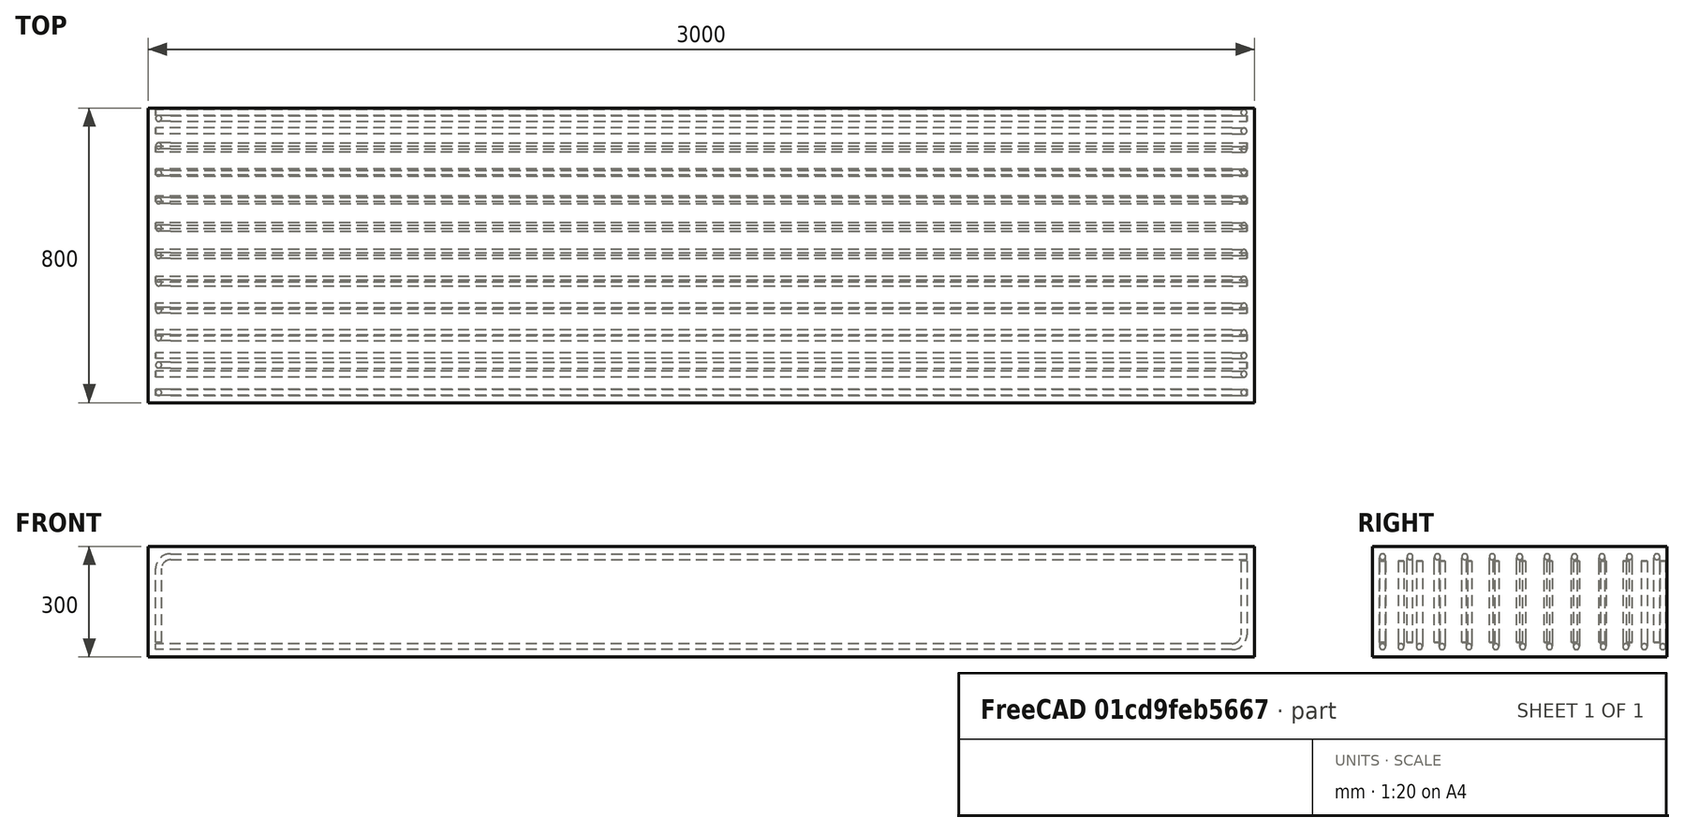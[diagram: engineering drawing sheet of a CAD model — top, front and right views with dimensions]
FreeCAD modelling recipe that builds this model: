
FCSTD DOCUMENT  (FreeCAD 0.19R20802 (Git))
Label: lshape_rebar_drawing_dimensioning
License: All rights reserved
LicenseURL: http://en.wikipedia.org/wiki/All_rights_reserved
objects: TechDraw::DrawViewSymbolPython×18, TechDraw::DrawSVGTemplate×6, TechDraw::DrawPage×6, Part::FeaturePython×3, Sketcher::SketchObject×2
note: 5 computed .brp shape members not serialized (recipe doc carries the construction recipe); baked Part::Feature solids carry a one-line shape summary decoded from their .brp

FEATURE [Part::FeaturePython] Structure  label="Footing"  # Arch/BIM 77 (typed FeaturePython)
  FaceMaker = 0
  Height = 300
  HorizontalArea = 2400000
  IfcData = attributes={"GlobalId": {"name": "GlobalId", "type": "IfcGloballyUniqueId", "is_enum": false, "enum_values": []}, "Description": {"... (+505 chars omitted),+1 more (map truncated)
  IfcType = 77
  Length = 3000
  MoveBase = false
  MoveWithHost = false
  Nodes = (2) [(0,0,5.55112e-16),(0,0,3000)]
  NodesOffset = 0
  Normal = (0,0,0)
  PerimeterLength = 7600
  PredefinedType = 1
  VerticalArea = 2280000
  Width = 800
FEATURE [Sketcher::SketchObject] Sketch
  MapMode = 5
  Placement = pos=(0,-400,0) rot=(1,0,0;1.5708rad)
  Support = -> [Structure]
  sketch-geometry (2):
    g0: LineSegment StartX=2972 StartY=110 StartZ=0 EndX=2972 EndY=-122 EndZ=0
    g1: LineSegment StartX=2972 StartY=-122 StartZ=0 EndX=20 EndY=-122 EndZ=0
FEATURE [Part::FeaturePython] Rebar  label="LShapeRebar"  # Arch/BIM 110 (typed FeaturePython)
  Amount = 13
  AmountCheck = false
  Base = -> Sketch
  BottomCover = 20
  CustomSpacing = 3@50.0+7@72.85714285714286+3@50.0
  Diameter = 16
  Direction = (0,0,0)
  Distance = 0
  FrontCover = 20
  HorizontalArea = 0
  Host = -> Structure
  IfcType = 110
  LeftCover = 20
  Length = 3184
  Mark = BRb
  MoveBase = false
  MoveWithHost = false
  OffsetEnd = 28
  OffsetStart = 28
  Orientation = Bottom Right
  PerimeterLength = 0
  PlacementList = 13 placements: [(0,28,-6.21725e-15),(0,78,-1.73195e-14),(0,128,-2.84217e-14),(0,189.429,-4.20616e-14),(0,262.286,-5.82391e-14),(0,335.143,-7.44167e-14),(0,408,-9.05942e-14),(0,480.857,-1.06772e-13),(0,553.714,-1.22949e-13),(0,626.571,-1.39127e-13),(0,688,-1.52767e-13),(0,738,-1.63869e-13),(0,788,-1.74971e-13)]
  RebarShape = 2
  RightCover = 20
  Rounding = 2
  Spacing = 0
  TopCover = 40
  TotalLength = 41392
  TrueSpacing = 50
  VerticalArea = 0
FEATURE [Sketcher::SketchObject] Sketch001
  MapMode = 5
  Placement = pos=(0,-400,0) rot=(1,0,0;1.5708rad)
  Support = -> [Structure]
  sketch-geometry (2):
    g0: LineSegment StartX=28 StartY=-110 StartZ=0 EndX=28 EndY=122 EndZ=0
    g1: LineSegment StartX=28 StartY=122 StartZ=0 EndX=2980 EndY=122 EndZ=0
FEATURE [Part::FeaturePython] Rebar001  label="LShapeRebar001"  # Arch/BIM 110 (typed FeaturePython)
  Amount = 11
  AmountCheck = false
  Base = -> Sketch001
  BottomCover = 40
  Diameter = 16
  Direction = (0,0,0)
  Distance = 0
  FrontCover = 20
  HorizontalArea = 0
  Host = -> Structure
  IfcType = 110
  LeftCover = 20
  Length = 3184
  Mark = TRb
  MoveBase = false
  MoveWithHost = false
  OffsetEnd = 28
  OffsetStart = 28
  Orientation = Top Left
  PerimeterLength = 0
  PlacementList = 11 placements: arithmetic series from (0,28,-6.21725e-15) step (0,74.4,-1.65201e-14) to (0,772,-1.71418e-13)
  RebarShape = 2
  RightCover = 20
  Rounding = 2
  Spacing = 74.4
  TopCover = 20
  TotalLength = 35024
  TrueSpacing = 70
  VerticalArea = 0
FEATURE [TechDraw::DrawSVGTemplate] Template
  Height = 210
  Orientation = 1
  Width = 297
FEATURE [TechDraw::DrawViewSymbolPython] ReinforcementDrawingView  label="Front View"  # drawing view (typed FeaturePython)
  DimensionBottomOffset = 16
  DimensionLeftOffset = 10
  DimensionRightOffset = 10
  DimensionTopOffset = 16
  Height = 300
  LeftOffset = 20
  LockPosition = false
  MaxHeight = 210
  MaxWidth = 297
  MinBottomOffset = 20
  MinRightOffset = 20
  PositionType = 0
  Rebars = -> [Rebar,Rebar001]
  RebarsColorStyle = 0
  RebarsStrokeWidth = 0.35
  Rotation = 0
  Scale = 0.0856667
  ScaleType = 1
  Structure = -> Structure
  StructureColorStyle = 0
  StructureStrokeWidth = 0.5
  Symbol = <blob: 3186 chars omitted>
  Template = -> Template
  TopOffset = 92.15
  View = 0
  VisibleRebars = -> [Rebar,Rebar001]
  Width = 3000
  X = 148.5
  Y = 105
  expr: TopOffset = .Template.Height.Value / 2 - .Height.Value * .Scale / 2
  expr: LeftOffset = .Template.Width.Value / 2 - .Width.Value * .Scale / 2
FEATURE [TechDraw::DrawViewSymbolPython] ReinforcementDimensioning  # drawing view (typed FeaturePython)
  DimensionBottomOffset = 10
  DimensionFormat = %M %C⌀%D,span=%S
  DimensionLeftOffset = 10
  DimensionRightOffset = 10
  DimensionTopOffset = 10
  Font = DejaVu Sans
  FontSize = 3
  LineEndSymbol = 0
  LineMidPointSymbol = 1
  LineStartSymbol = 3
  LineStyle = 0
  LockPosition = false
  MultiRebar_LineEndSymbol = 0
  MultiRebar_LineStartSymbol = 0
  MultiRebar_OuterDimension = true
  MultiRebar_TextPositionType = 0
  ParentDrawingView = -> ReinforcementDrawingView
  Rebar = -> Rebar
  Rotation = 0
  Scale = 0.0856667
  ScaleType = 2
  SingleRebar_LineEndSymbol = 0
  SingleRebar_LineStartSymbol = 3
  SingleRebar_OuterDimension = false
  SingleRebar_TextPositionType = 1
  StrokeWidth = 0.25
  Symbol = <svg version="1.1" xmlns="http://www.w3.org/2000/svg" xmlns:xlink="http://www.w3.org/1999/xlink" xmlns:freecad="http://www.freecadweb.org/wiki/index.php?title=Svg_Namespace" width="3000.0mm" height="300.0mm" viewBox="0 0 3000.0 300.0"><g transform="translate(0.0, 150.00000000000065)"><g><path d="M609.0 266.7315175097276 L609.0 121.99999999999966" style="stroke:#00007f;stroke-width:2.9182879377431905;stroke-linecap:round;fill:none;" stroke-dasharray="" /><g id="line_mid_points" /><path d="M0,0 -8,-1.5 V1.5 L0,0" style="stroke:#00007f;fill:#00007f;stroke-width:2.9182879377431905;stroke-linecap:round;stroke-linejoin:bevel;" transform="translate(609.0 121.99999999999966) rotate(-90.0 0 0)" /></g><text x="609.0" y="284.24124513618676" style="white-space:pre;" fill="#005400" font-family="DejaVu Sans" font-size="35.019455252918284" text-anchor="middle" dominant-baseline="baseline" xml:space="preserve">BRb 13⌀16,span=760</text></g></svg>
  TextPositionType = 0
  WayPoints = (2) [(0,0,0),(50,0,0)]
  WayPointsType = 0
  X = 148.5
  Y = 105
FEATURE [TechDraw::DrawViewSymbolPython] ReinforcementDimensioning001  # drawing view (typed FeaturePython)
  DimensionBottomOffset = 16
  DimensionFormat = %M %C⌀%D,span=%S
  DimensionLeftOffset = 10
  DimensionRightOffset = 10
  DimensionTopOffset = 10
  Font = DejaVu Sans
  FontSize = 3
  LineEndSymbol = 0
  LineMidPointSymbol = 1
  LineStartSymbol = 3
  LineStyle = 0
  LockPosition = false
  MultiRebar_LineEndSymbol = 0
  MultiRebar_LineStartSymbol = 0
  MultiRebar_OuterDimension = true
  MultiRebar_TextPositionType = 0
  ParentDrawingView = -> ReinforcementDrawingView
  Rebar = -> Rebar001
  Rotation = 0
  Scale = 0.0856667
  ScaleType = 2
  SingleRebar_LineEndSymbol = 0
  SingleRebar_LineStartSymbol = 3
  SingleRebar_OuterDimension = false
  SingleRebar_TextPositionType = 1
  StrokeWidth = 0.25
  Symbol = <svg version="1.1" xmlns="http://www.w3.org/2000/svg" xmlns:xlink="http://www.w3.org/1999/xlink" xmlns:freecad="http://www.freecadweb.org/wiki/index.php?title=Svg_Namespace" width="3000.0mm" height="300.0mm" viewBox="0 0 3000.0 300.0"><g transform="translate(0.0, 150.00000000000065)"><g><path d="M2530.0 -266.7315175097283 L2530.0 -122.00000000000034" style="stroke:#00007f;stroke-width:2.9182879377431905;stroke-linecap:round;fill:none;" stroke-dasharray="" /><g id="line_mid_points" /><path d="M0,0 -8,-1.5 V1.5 L0,0" style="stroke:#00007f;fill:#00007f;stroke-width:2.9182879377431905;stroke-linecap:round;stroke-linejoin:bevel;" transform="translate(2530.0 -122.00000000000034) rotate(90.0 0 0)" /></g><text x="2530.0" y="-266.7315175097283" style="white-space:pre;" fill="#005400" font-family="DejaVu Sans" font-size="35.019455252918284" text-anchor="middle" dominant-baseline="baseline" xml:space="preserve">TRb 11⌀16,span=744</text></g></svg>
  TextPositionType = 0
  WayPoints = (2) [(0,0,0),(50,0,0)]
  WayPointsType = 0
  X = 148.5
  Y = 105
FEATURE [TechDraw::DrawPage] TechDraw__DrawPage  label="Footing Drawing"
  KeepUpdated = true
  NextBalloonIndex = 1
  ProjectionType = 0
  Template = -> Template
  Views = -> [ReinforcementDrawingView,ReinforcementDimensioning,ReinforcementDimensioning001]
FEATURE [TechDraw::DrawSVGTemplate] Template001
  Height = 210
  Orientation = 1
  Width = 297
FEATURE [TechDraw::DrawViewSymbolPython] ReinforcementDrawingView001  label="Rear View"  # drawing view (typed FeaturePython)
  DimensionBottomOffset = 16
  DimensionLeftOffset = 10
  DimensionRightOffset = 10
  DimensionTopOffset = 16
  Height = 300
  LeftOffset = 20
  LockPosition = false
  MaxHeight = 210
  MaxWidth = 297
  MinBottomOffset = 20
  MinRightOffset = 20
  PositionType = 0
  Rebars = -> [Rebar,Rebar001]
  RebarsColorStyle = 0
  RebarsStrokeWidth = 0.35
  Rotation = 0
  Scale = 0.0856667
  ScaleType = 1
  Structure = -> Structure
  StructureColorStyle = 0
  StructureStrokeWidth = 0.5
  Symbol = <blob: 3214 chars omitted>
  Template = -> Template001
  TopOffset = 92.15
  View = 1
  VisibleRebars = -> [Rebar,Rebar001]
  Width = 3000
  X = 148.5
  Y = 105
  expr: TopOffset = .Template.Height.Value / 2 - .Height.Value * .Scale / 2
  expr: LeftOffset = .Template.Width.Value / 2 - .Width.Value * .Scale / 2
FEATURE [TechDraw::DrawViewSymbolPython] ReinforcementDimensioning002  # drawing view (typed FeaturePython)
  DimensionBottomOffset = 10
  DimensionFormat = %M %C⌀%D,span=%S
  DimensionLeftOffset = 10
  DimensionRightOffset = 10
  DimensionTopOffset = 10
  Font = DejaVu Sans
  FontSize = 3
  LineEndSymbol = 0
  LineMidPointSymbol = 1
  LineStartSymbol = 3
  LineStyle = 0
  LockPosition = false
  MultiRebar_LineEndSymbol = 0
  MultiRebar_LineStartSymbol = 0
  MultiRebar_OuterDimension = true
  MultiRebar_TextPositionType = 0
  ParentDrawingView = -> ReinforcementDrawingView001
  Rebar = -> Rebar
  Rotation = 0
  Scale = 0.0856667
  ScaleType = 2
  SingleRebar_LineEndSymbol = 0
  SingleRebar_LineStartSymbol = 3
  SingleRebar_OuterDimension = false
  SingleRebar_TextPositionType = 1
  StrokeWidth = 0.25
  Symbol = <svg version="1.1" xmlns="http://www.w3.org/2000/svg" xmlns:xlink="http://www.w3.org/1999/xlink" xmlns:freecad="http://www.freecadweb.org/wiki/index.php?title=Svg_Namespace" width="3000.0mm" height="300.0mm" viewBox="0 0 3000.0 300.0"><g transform="translate(3000.0, 150.00000000000065)"><g><path d="M-1851.0 266.7315175097276 L-1851.0 121.99999999999966" style="stroke:#00007f;stroke-width:2.9182879377431905;stroke-linecap:round;fill:none;" stroke-dasharray="" /><g id="line_mid_points" /><path d="M0,0 -8,-1.5 V1.5 L0,0" style="stroke:#00007f;fill:#00007f;stroke-width:2.9182879377431905;stroke-linecap:round;stroke-linejoin:bevel;" transform="translate(-1851.0 121.99999999999966) rotate(-90.0 0 0)" /></g><text x="-1851.0" y="284.24124513618676" style="white-space:pre;" fill="#005400" font-family="DejaVu Sans" font-size="35.019455252918284" text-anchor="middle" dominant-baseline="baseline" xml:space="preserve">BRb 13⌀16,span=760</text></g></svg>
  TextPositionType = 0
  WayPoints = (2) [(0,0,0),(50,0,0)]
  WayPointsType = 0
  X = 148.5
  Y = 105
FEATURE [TechDraw::DrawViewSymbolPython] ReinforcementDimensioning003  # drawing view (typed FeaturePython)
  DimensionBottomOffset = 16
  DimensionFormat = %M %C⌀%D,span=%S
  DimensionLeftOffset = 10
  DimensionRightOffset = 10
  DimensionTopOffset = 10
  Font = DejaVu Sans
  FontSize = 3
  LineEndSymbol = 0
  LineMidPointSymbol = 1
  LineStartSymbol = 3
  LineStyle = 0
  LockPosition = false
  MultiRebar_LineEndSymbol = 0
  MultiRebar_LineStartSymbol = 0
  MultiRebar_OuterDimension = true
  MultiRebar_TextPositionType = 0
  ParentDrawingView = -> ReinforcementDrawingView001
  Rebar = -> Rebar001
  Rotation = 0
  Scale = 0.0856667
  ScaleType = 2
  SingleRebar_LineEndSymbol = 0
  SingleRebar_LineStartSymbol = 3
  SingleRebar_OuterDimension = false
  SingleRebar_TextPositionType = 1
  StrokeWidth = 0.25
  Symbol = <svg version="1.1" xmlns="http://www.w3.org/2000/svg" xmlns:xlink="http://www.w3.org/1999/xlink" xmlns:freecad="http://www.freecadweb.org/wiki/index.php?title=Svg_Namespace" width="3000.0mm" height="300.0mm" viewBox="0 0 3000.0 300.0"><g transform="translate(3000.0, 150.00000000000065)"><g><path d="M-2870.0 -266.7315175097283 L-2870.0 -122.00000000000034" style="stroke:#00007f;stroke-width:2.9182879377431905;stroke-linecap:round;fill:none;" stroke-dasharray="" /><g id="line_mid_points" /><path d="M0,0 -8,-1.5 V1.5 L0,0" style="stroke:#00007f;fill:#00007f;stroke-width:2.9182879377431905;stroke-linecap:round;stroke-linejoin:bevel;" transform="translate(-2870.0 -122.00000000000034) rotate(90.0 0 0)" /></g><text x="-2870.0" y="-266.7315175097283" style="white-space:pre;" fill="#005400" font-family="DejaVu Sans" font-size="35.019455252918284" text-anchor="middle" dominant-baseline="baseline" xml:space="preserve">TRb 11⌀16,span=744</text></g></svg>
  TextPositionType = 0
  WayPoints = (2) [(0,0,0),(50,0,0)]
  WayPointsType = 0
  X = 148.5
  Y = 105
FEATURE [TechDraw::DrawPage] TechDraw__DrawPage001  label="Footing Drawing001"
  KeepUpdated = true
  NextBalloonIndex = 1
  ProjectionType = 0
  Template = -> Template001
  Views = -> [ReinforcementDrawingView001,ReinforcementDimensioning002,ReinforcementDimensioning003]
FEATURE [TechDraw::DrawSVGTemplate] Template002
  Height = 210
  Orientation = 1
  Width = 297
FEATURE [TechDraw::DrawViewSymbolPython] ReinforcementDrawingView002  label="Left View"  # drawing view (typed FeaturePython)
  DimensionBottomOffset = 16
  DimensionLeftOffset = 10
  DimensionRightOffset = 10
  DimensionTopOffset = 16
  Height = 300
  LeftOffset = 20
  LockPosition = false
  MaxHeight = 210
  MaxWidth = 297
  MinBottomOffset = 20
  MinRightOffset = 20
  PositionType = 0
  Rebars = -> [Rebar,Rebar001]
  RebarsColorStyle = 0
  RebarsStrokeWidth = 0.35
  Rotation = 0
  Scale = 0.32125
  ScaleType = 1
  Structure = -> Structure
  StructureColorStyle = 0
  StructureStrokeWidth = 0.5
  Symbol = <blob: 9738 chars omitted>
  Template = -> Template002
  TopOffset = 56.8125
  View = 2
  VisibleRebars = -> [Rebar,Rebar001]
  Width = 800
  X = 148.5
  Y = 105
  expr: TopOffset = .Template.Height.Value / 2 - .Height.Value * .Scale / 2
  expr: LeftOffset = .Template.Width.Value / 2 - .Width.Value * .Scale / 2
FEATURE [TechDraw::DrawViewSymbolPython] ReinforcementDimensioning004  # drawing view (typed FeaturePython)
  DimensionBottomOffset = 10
  DimensionFormat = %M %C⌀%D,span=%S
  DimensionLeftOffset = 10
  DimensionRightOffset = 10
  DimensionTopOffset = 10
  Font = DejaVu Sans
  FontSize = 3
  LineEndSymbol = 0
  LineMidPointSymbol = 1
  LineStartSymbol = 3
  LineStyle = 0
  LockPosition = false
  MultiRebar_LineEndSymbol = 0
  MultiRebar_LineStartSymbol = 0
  MultiRebar_OuterDimension = true
  MultiRebar_TextPositionType = 0
  ParentDrawingView = -> ReinforcementDrawingView002
  Rebar = -> Rebar
  Rotation = 0
  Scale = 0.32125
  ScaleType = 2
  SingleRebar_LineEndSymbol = 0
  SingleRebar_LineStartSymbol = 3
  SingleRebar_OuterDimension = false
  SingleRebar_TextPositionType = 1
  StrokeWidth = 0.25
  Symbol = <blob: 5461 chars omitted>
  TextPositionType = 0
  WayPoints = (2) [(0,0,0),(50,0,0)]
  WayPointsType = 0
  X = 148.5
  Y = 105
FEATURE [TechDraw::DrawViewSymbolPython] ReinforcementDimensioning005  # drawing view (typed FeaturePython)
  DimensionBottomOffset = 16
  DimensionFormat = %M %C⌀%D,span=%S
  DimensionLeftOffset = 10
  DimensionRightOffset = 10
  DimensionTopOffset = 10
  Font = DejaVu Sans
  FontSize = 3
  LineEndSymbol = 0
  LineMidPointSymbol = 1
  LineStartSymbol = 3
  LineStyle = 0
  LockPosition = false
  MultiRebar_LineEndSymbol = 0
  MultiRebar_LineStartSymbol = 0
  MultiRebar_OuterDimension = true
  MultiRebar_TextPositionType = 0
  ParentDrawingView = -> ReinforcementDrawingView002
  Rebar = -> Rebar001
  Rotation = 0
  Scale = 0.32125
  ScaleType = 2
  SingleRebar_LineEndSymbol = 0
  SingleRebar_LineStartSymbol = 3
  SingleRebar_OuterDimension = false
  SingleRebar_TextPositionType = 1
  StrokeWidth = 0.25
  Symbol = <blob: 3041 chars omitted>
  TextPositionType = 0
  WayPoints = (2) [(0,0,0),(50,0,0)]
  WayPointsType = 0
  X = 148.5
  Y = 105
FEATURE [TechDraw::DrawPage] TechDraw__DrawPage002  label="Footing Drawing002"
  KeepUpdated = true
  NextBalloonIndex = 1
  ProjectionType = 0
  Template = -> Template002
  Views = -> [ReinforcementDrawingView002,ReinforcementDimensioning004,ReinforcementDimensioning005]
FEATURE [TechDraw::DrawSVGTemplate] Template003
  Height = 210
  Orientation = 1
  Width = 297
FEATURE [TechDraw::DrawViewSymbolPython] ReinforcementDrawingView003  label="Right View"  # drawing view (typed FeaturePython)
  DimensionBottomOffset = 16
  DimensionLeftOffset = 10
  DimensionRightOffset = 10
  DimensionTopOffset = 16
  Height = 300
  LeftOffset = 20
  LockPosition = false
  MaxHeight = 210
  MaxWidth = 297
  MinBottomOffset = 20
  MinRightOffset = 20
  PositionType = 0
  Rebars = -> [Rebar,Rebar001]
  RebarsColorStyle = 0
  RebarsStrokeWidth = 0.35
  Rotation = 0
  Scale = 0.32125
  ScaleType = 1
  Structure = -> Structure
  StructureColorStyle = 0
  StructureStrokeWidth = 0.5
  Symbol = <blob: 9733 chars omitted>
  Template = -> Template003
  TopOffset = 56.8125
  View = 3
  VisibleRebars = -> [Rebar,Rebar001]
  Width = 800
  X = 148.5
  Y = 105
  expr: TopOffset = .Template.Height.Value / 2 - .Height.Value * .Scale / 2
  expr: LeftOffset = .Template.Width.Value / 2 - .Width.Value * .Scale / 2
FEATURE [TechDraw::DrawViewSymbolPython] ReinforcementDimensioning006  # drawing view (typed FeaturePython)
  DimensionBottomOffset = 10
  DimensionFormat = %M %C⌀%D,span=%S
  DimensionLeftOffset = 10
  DimensionRightOffset = 10
  DimensionTopOffset = 10
  Font = DejaVu Sans
  FontSize = 3
  LineEndSymbol = 0
  LineMidPointSymbol = 1
  LineStartSymbol = 3
  LineStyle = 0
  LockPosition = false
  MultiRebar_LineEndSymbol = 0
  MultiRebar_LineStartSymbol = 0
  MultiRebar_OuterDimension = true
  MultiRebar_TextPositionType = 0
  ParentDrawingView = -> ReinforcementDrawingView003
  Rebar = -> Rebar
  Rotation = 0
  Scale = 0.32125
  ScaleType = 2
  SingleRebar_LineEndSymbol = 0
  SingleRebar_LineStartSymbol = 3
  SingleRebar_OuterDimension = false
  SingleRebar_TextPositionType = 1
  StrokeWidth = 0.25
  Symbol = <blob: 5434 chars omitted>
  TextPositionType = 0
  WayPoints = (2) [(0,0,0),(50,0,0)]
  WayPointsType = 0
  X = 148.5
  Y = 105
FEATURE [TechDraw::DrawViewSymbolPython] ReinforcementDimensioning007  # drawing view (typed FeaturePython)
  DimensionBottomOffset = 16
  DimensionFormat = %M %C⌀%D,span=%S
  DimensionLeftOffset = 10
  DimensionRightOffset = 10
  DimensionTopOffset = 10
  Font = DejaVu Sans
  FontSize = 3
  LineEndSymbol = 0
  LineMidPointSymbol = 1
  LineStartSymbol = 3
  LineStyle = 0
  LockPosition = false
  MultiRebar_LineEndSymbol = 0
  MultiRebar_LineStartSymbol = 0
  MultiRebar_OuterDimension = true
  MultiRebar_TextPositionType = 0
  ParentDrawingView = -> ReinforcementDrawingView003
  Rebar = -> Rebar001
  Rotation = 0
  Scale = 0.32125
  ScaleType = 2
  SingleRebar_LineEndSymbol = 0
  SingleRebar_LineStartSymbol = 3
  SingleRebar_OuterDimension = false
  SingleRebar_TextPositionType = 1
  StrokeWidth = 0.25
  Symbol = <blob: 3020 chars omitted>
  TextPositionType = 0
  WayPoints = (2) [(0,0,0),(50,0,0)]
  WayPointsType = 0
  X = 148.5
  Y = 105
FEATURE [TechDraw::DrawPage] TechDraw__DrawPage003  label="Footing Drawing003"
  KeepUpdated = true
  NextBalloonIndex = 1
  ProjectionType = 0
  Template = -> Template003
  Views = -> [ReinforcementDrawingView003,ReinforcementDimensioning006,ReinforcementDimensioning007]
FEATURE [TechDraw::DrawSVGTemplate] Template004
  Height = 210
  Orientation = 1
  Width = 297
FEATURE [TechDraw::DrawViewSymbolPython] ReinforcementDrawingView004  label="Top View"  # drawing view (typed FeaturePython)
  DimensionBottomOffset = 10
  DimensionLeftOffset = 16
  DimensionRightOffset = 16
  DimensionTopOffset = 10
  Height = 800
  LeftOffset = 10
  LockPosition = false
  MaxHeight = 210
  MaxWidth = 297
  MinBottomOffset = 20
  MinRightOffset = 10
  PositionType = 0
  Rebars = -> [Rebar,Rebar001]
  RebarsColorStyle = 0
  RebarsStrokeWidth = 0.35
  Rotation = 0
  Scale = 0.0923333
  ScaleType = 1
  Structure = -> Structure
  StructureColorStyle = 0
  StructureStrokeWidth = 0.5
  Symbol = <blob: 9500 chars omitted>
  Template = -> Template004
  TopOffset = 69.4
  View = 4
  VisibleRebars = -> [Rebar,Rebar001]
  Width = 3000
  X = 148.5
  Y = 103.667
  expr: TopOffset = .Template.Height.Value / 2 - .Height.Value * .Scale / 2
FEATURE [TechDraw::DrawViewSymbolPython] ReinforcementDimensioning008  # drawing view (typed FeaturePython)
  DimensionBottomOffset = 10
  DimensionFormat = %M %C⌀%D,sp=%S
  DimensionLeftOffset = 10
  DimensionRightOffset = 10
  DimensionTopOffset = 10
  Font = DejaVu Sans
  FontSize = 3
  LineEndSymbol = 0
  LineMidPointSymbol = 1
  LineStartSymbol = 3
  LineStyle = 0
  LockPosition = false
  MultiRebar_LineEndSymbol = 0
  MultiRebar_LineStartSymbol = 0
  MultiRebar_OuterDimension = true
  MultiRebar_TextPositionType = 0
  ParentDrawingView = -> ReinforcementDrawingView004
  Rebar = -> Rebar
  Rotation = 0
  Scale = 0.0923333
  ScaleType = 2
  SingleRebar_LineEndSymbol = 0
  SingleRebar_LineStartSymbol = 3
  SingleRebar_OuterDimension = false
  SingleRebar_TextPositionType = 1
  StrokeWidth = 0.25
  Symbol = <blob: 5483 chars omitted>
  TextPositionType = 0
  WayPoints = (2) [(0,0,0),(50,0,0)]
  WayPointsType = 0
  X = 148.5
  Y = 103.667
FEATURE [TechDraw::DrawViewSymbolPython] ReinforcementDimensioning009  # drawing view (typed FeaturePython)
  DimensionBottomOffset = 10
  DimensionFormat = %M %C⌀%D,span=%S
  DimensionLeftOffset = 16
  DimensionRightOffset = 10
  DimensionTopOffset = 10
  Font = DejaVu Sans
  FontSize = 3
  LineEndSymbol = 0
  LineMidPointSymbol = 1
  LineStartSymbol = 3
  LineStyle = 0
  LockPosition = false
  MultiRebar_LineEndSymbol = 0
  MultiRebar_LineStartSymbol = 0
  MultiRebar_OuterDimension = true
  MultiRebar_TextPositionType = 0
  ParentDrawingView = -> ReinforcementDrawingView004
  Rebar = -> Rebar001
  Rotation = 0
  Scale = 0.0923333
  ScaleType = 2
  SingleRebar_LineEndSymbol = 0
  SingleRebar_LineStartSymbol = 3
  SingleRebar_OuterDimension = false
  SingleRebar_TextPositionType = 1
  StrokeWidth = 0.25
  Symbol = <blob: 2996 chars omitted>
  TextPositionType = 0
  WayPoints = (2) [(0,0,0),(50,0,0)]
  WayPointsType = 0
  X = 148.5
  Y = 103.667
FEATURE [TechDraw::DrawPage] TechDraw__DrawPage004  label="Footing Drawing004"
  KeepUpdated = true
  NextBalloonIndex = 1
  ProjectionType = 0
  Template = -> Template004
  Views = -> [ReinforcementDrawingView004,ReinforcementDimensioning008,ReinforcementDimensioning009]
FEATURE [TechDraw::DrawSVGTemplate] Template005
  Height = 210
  Orientation = 1
  Width = 297
FEATURE [TechDraw::DrawViewSymbolPython] ReinforcementDrawingView005  label="Bottom View"  # drawing view (typed FeaturePython)
  DimensionBottomOffset = 10
  DimensionLeftOffset = 16
  DimensionRightOffset = 16
  DimensionTopOffset = 10
  Height = 800
  LeftOffset = 10
  LockPosition = false
  MaxHeight = 210
  MaxWidth = 297
  MinBottomOffset = 20
  MinRightOffset = 10
  PositionType = 0
  Rebars = -> [Rebar,Rebar001]
  RebarsColorStyle = 0
  RebarsStrokeWidth = 0.35
  Rotation = 0
  Scale = 0.0923333
  ScaleType = 1
  Structure = -> Structure
  StructureColorStyle = 0
  StructureStrokeWidth = 0.5
  Symbol = <blob: 9495 chars omitted>
  Template = -> Template005
  TopOffset = 68.0667
  View = 5
  VisibleRebars = -> [Rebar,Rebar001]
  Width = 3000
  X = 148.5
  Y = 105
  expr: TopOffset = .Template.Height.Value / 2 - .Height.Value * .Scale / 2
FEATURE [TechDraw::DrawViewSymbolPython] ReinforcementDimensioning010  # drawing view (typed FeaturePython)
  DimensionBottomOffset = 10
  DimensionFormat = %M %C⌀%D,sp=%S
  DimensionLeftOffset = 10
  DimensionRightOffset = 10
  DimensionTopOffset = 10
  Font = DejaVu Sans
  FontSize = 3
  LineEndSymbol = 0
  LineMidPointSymbol = 1
  LineStartSymbol = 3
  LineStyle = 0
  LockPosition = false
  MultiRebar_LineEndSymbol = 0
  MultiRebar_LineStartSymbol = 0
  MultiRebar_OuterDimension = true
  MultiRebar_TextPositionType = 0
  ParentDrawingView = -> ReinforcementDrawingView005
  Rebar = -> Rebar
  Rotation = 0
  Scale = 0.0923333
  ScaleType = 2
  SingleRebar_LineEndSymbol = 0
  SingleRebar_LineStartSymbol = 3
  SingleRebar_OuterDimension = false
  SingleRebar_TextPositionType = 1
  StrokeWidth = 0.25
  Symbol = <blob: 5469 chars omitted>
  TextPositionType = 0
  WayPoints = (2) [(0,0,0),(50,0,0)]
  WayPointsType = 0
  X = 148.5
  Y = 105
FEATURE [TechDraw::DrawViewSymbolPython] ReinforcementDimensioning011  # drawing view (typed FeaturePython)
  DimensionBottomOffset = 10
  DimensionFormat = %M %C⌀%D,span=%S
  DimensionLeftOffset = 16
  DimensionRightOffset = 10
  DimensionTopOffset = 10
  Font = DejaVu Sans
  FontSize = 3
  LineEndSymbol = 0
  LineMidPointSymbol = 1
  LineStartSymbol = 3
  LineStyle = 0
  LockPosition = false
  MultiRebar_LineEndSymbol = 0
  MultiRebar_LineStartSymbol = 0
  MultiRebar_OuterDimension = true
  MultiRebar_TextPositionType = 0
  ParentDrawingView = -> ReinforcementDrawingView005
  Rebar = -> Rebar001
  Rotation = 0
  Scale = 0.0923333
  ScaleType = 2
  SingleRebar_LineEndSymbol = 0
  SingleRebar_LineStartSymbol = 3
  SingleRebar_OuterDimension = false
  SingleRebar_TextPositionType = 1
  StrokeWidth = 0.25
  Symbol = <blob: 2986 chars omitted>
  TextPositionType = 0
  WayPoints = (2) [(0,0,0),(50,0,0)]
  WayPointsType = 0
  X = 148.5
  Y = 105
FEATURE [TechDraw::DrawPage] TechDraw__DrawPage005  label="Footing Drawing005"
  KeepUpdated = true
  NextBalloonIndex = 1
  ProjectionType = 0
  Template = -> Template005
  Views = -> [ReinforcementDrawingView005,ReinforcementDimensioning010,ReinforcementDimensioning011]
